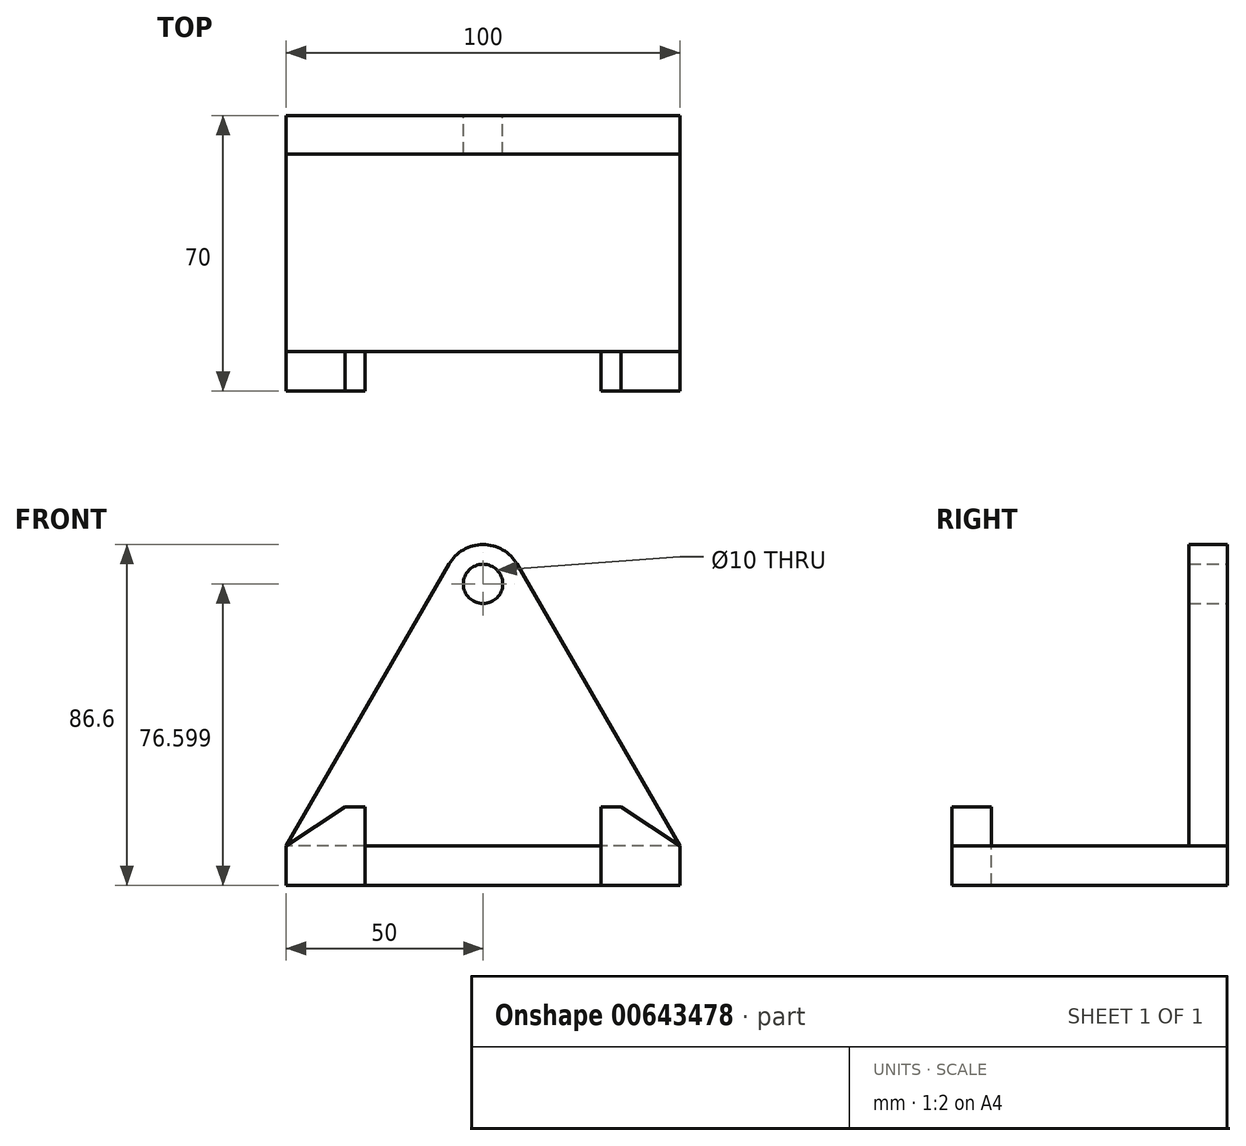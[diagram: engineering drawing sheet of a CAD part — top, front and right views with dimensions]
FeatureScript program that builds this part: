
annotation { "Feature Type Name" : "Feature", "Feature Type Description" : "" }
export const myFeature = defineFeature(function(context is Context, id is Id, definition is map)
    precondition{}
    {
        {
            var Q0;
            Q0=qCreatedBy(makeId("Front.planeOp"),FACE);
            var sketch = newSketch(context, id + "F0", { "sketchPlane" : qUnion([Q0])});
            skArc(sketch, "E0", {"start": v(8.66, 47.06) * mm, "mid": v(0, 52.06) * mm, "end": v(-8.66, 47.06) * mm});
            skCircle(sketch, "E1", {"center": v(0, 42.06) * mm, "radius": 5 * mm});
            skLineSegment(sketch, "E2", {"start": v(-50, -24.54) * mm, "end": v(50, -24.54) * mm});
            skLineSegment(sketch, "E3", {"start": v(50, -24.54) * mm, "end": v(8.66, 47.06) * mm});
            skLineSegment(sketch, "E4", {"start": v(-8.66, 47.06) * mm, "end": v(-50, -24.54) * mm});
            skSolve(sketch);
        }
        {
            var Q0;
            Q0 = qSketchRegion(id + "F0", true);
            extrude(context, id + "F1", {"entities" : qUnion([Q0]), "depth" : 9.8 * mm, "offsetDistance" : 25 * mm});
        }
        {
            var Q0;
            Q0=makeQuery(id+"F1.opExtrude","SWEPT_FACE",FACE,{"disambiguationData":[OSD([sQuery(id+"F0.wireOp",EDGE,"E2")])]});
            var sketch = newSketch(context, id + "F2", { "sketchPlane" : qUnion([Q0])});
            skLineSegment(sketch, "E5", {"start": v(-50, 0) * mm, "end": v(-50, 60) * mm});
            skLineSegment(sketch, "E6", {"start": v(50, 0) * mm, "end": v(50, 60) * mm});
            skLineSegment(sketch, "E7", {"start": v(50, 60) * mm, "end": v(-50, 60) * mm});
            skLineSegment(sketch, "E8", {"start": v(-50, 0) * mm, "end": v(50, 0) * mm});
            skSolve(sketch);
        }
        {
            var Q0;
            Q0 = qSketchRegion(id + "F2", true);
            extrude(context, id + "F3", {"entities" : qUnion([Q0]), "operationType" : NewBodyOperationType.ADD, "depth" : 10 * mm, "offsetDistance" : 25 * mm});
        }
        {
            var Q0;
            Q0=makeQuery(id+"F3.opExtrude","SWEPT_FACE",FACE,{"disambiguationData":[OSD([sQuery(id+"F2.wireOp",EDGE,"E7")])]});
            var sketch = newSketch(context, id + "F4", { "sketchPlane" : qUnion([Q0])});
            skLineSegment(sketch, "E9", {"start": v(-50, -24.54) * mm, "end": v(-50, -34.54) * mm});
            skLineSegment(sketch, "E10", {"start": v(-50, -34.54) * mm, "end": v(-30, -34.54) * mm});
            skLineSegment(sketch, "E11", {"start": v(-30, -34.54) * mm, "end": v(-30, -14.54) * mm});
            skLineSegment(sketch, "E12", {"start": v(-30, -14.54) * mm, "end": v(-35, -14.54) * mm});
            skLineSegment(sketch, "E13", {"start": v(-50, -24.54) * mm, "end": v(-35, -14.54) * mm});
            skLineSegment(sketch, "E14", {"start": v(50, -24.54) * mm, "end": v(50, -34.54) * mm});
            skLineSegment(sketch, "E15", {"start": v(50, -34.54) * mm, "end": v(30, -34.54) * mm});
            skLineSegment(sketch, "E16", {"start": v(30, -34.54) * mm, "end": v(30, -14.54) * mm});
            skLineSegment(sketch, "E17", {"start": v(30, -14.54) * mm, "end": v(35, -14.54) * mm});
            skLineSegment(sketch, "E18", {"start": v(35, -14.54) * mm, "end": v(50, -24.54) * mm});
            skSolve(sketch);
        }
        {
            var Q0;
            Q0 = qSketchRegion(id + "F4", true);
            extrude(context, id + "F5", {"entities" : qUnion([Q0]), "operationType" : NewBodyOperationType.ADD, "depth" : 10 * mm, "offsetDistance" : 25 * mm});
        }
    });
